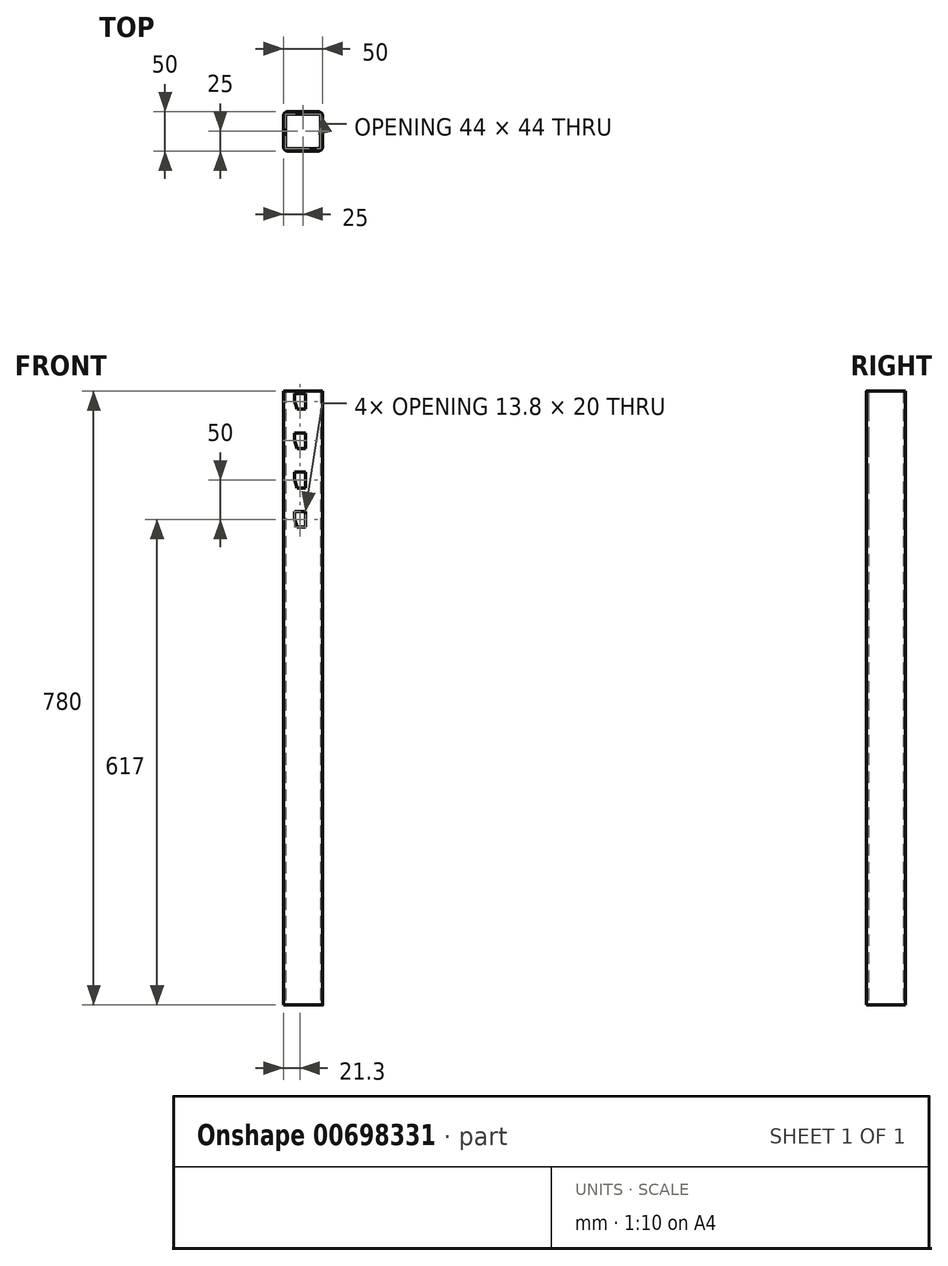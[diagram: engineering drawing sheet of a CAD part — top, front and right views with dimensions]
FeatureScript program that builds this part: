
annotation { "Feature Type Name" : "Feature", "Feature Type Description" : "" }
export const myFeature = defineFeature(function(context is Context, id is Id, definition is map)
    precondition{}
    {
        {
            var Q0;
            Q0=qCreatedBy(makeId("Top.planeOp"),FACE);
            var sketch = newSketch(context, id + "F0", { "sketchPlane" : qUnion([Q0])});
            skLineSegment(sketch, "E0.bottom", {"start": v(19, -25) * mm, "end": v(-19, -25) * mm});
            skLineSegment(sketch, "E0.top", {"start": v(19, 25) * mm, "end": v(-19, 25) * mm});
            skLineSegment(sketch, "E0.left", {"start": v(25, -19) * mm, "end": v(25, 19) * mm});
            skLineSegment(sketch, "E0.right", {"start": v(-25, -19) * mm, "end": v(-25, 19) * mm});
            skPoint(sketch, "E0.middle", {"position": v(0, 0) * mm});
            skLineSegment(sketch, "E1.bottom", {"start": v(19, 22) * mm, "end": v(-19, 22) * mm});
            skLineSegment(sketch, "E1.top", {"start": v(19, -22) * mm, "end": v(-19, -22) * mm});
            skLineSegment(sketch, "E1.left", {"start": v(22, 19) * mm, "end": v(22, -19) * mm});
            skLineSegment(sketch, "E1.right", {"start": v(-22, 19) * mm, "end": v(-22, -19) * mm});
            skPoint(sketch, "E2.visualSharp", {"position": v(-25, -25) * mm});
            skArc(sketch, "E2.filletArc", {"start": v(-25, -19) * mm, "mid": v(-23.24, -23.24) * mm, "end": v(-19, -25) * mm});
            skPoint(sketch, "E3.visualSharp", {"position": v(25, -25) * mm});
            skArc(sketch, "E3.filletArc", {"start": v(19, -25) * mm, "mid": v(23.24, -23.24) * mm, "end": v(25, -19) * mm});
            skPoint(sketch, "E4.visualSharp", {"position": v(25, 25) * mm});
            skArc(sketch, "E4.filletArc", {"start": v(25, 19) * mm, "mid": v(23.24, 23.24) * mm, "end": v(19, 25) * mm});
            skPoint(sketch, "E5.visualSharp", {"position": v(-25, 25) * mm});
            skArc(sketch, "E5.filletArc", {"start": v(-19, 25) * mm, "mid": v(-23.24, 23.24) * mm, "end": v(-25, 19) * mm});
            skPoint(sketch, "E6.visualSharp", {"position": v(-22, 22) * mm});
            skArc(sketch, "E6.filletArc", {"start": v(-19, 22) * mm, "mid": v(-21.12, 21.12) * mm, "end": v(-22, 19) * mm});
            skPoint(sketch, "E7.visualSharp", {"position": v(22, 22) * mm});
            skArc(sketch, "E7.filletArc", {"start": v(22, 19) * mm, "mid": v(21.12, 21.12) * mm, "end": v(19, 22) * mm});
            skPoint(sketch, "E8.visualSharp", {"position": v(22, -22) * mm});
            skArc(sketch, "E8.filletArc", {"start": v(19, -22) * mm, "mid": v(21.12, -21.12) * mm, "end": v(22, -19) * mm});
            skPoint(sketch, "E9.visualSharp", {"position": v(-22, -22) * mm});
            skArc(sketch, "E9.filletArc", {"start": v(-22, -19) * mm, "mid": v(-21.12, -21.12) * mm, "end": v(-19, -22) * mm});
            skSolve(sketch);
        }
        {
            var Q0;
            Q0=makeQuery(id+"F0.imprint","IMPRINT",FACE,{"disambiguationData":[TD([[makeQuery(id+"F0.imprint","IMPRINT",EDGE,{"derivedFrom":sQuery(id+"F0.wireOp",EDGE,"E0.bottom")}),-1.0]])]});
            extrude(context, id + "F1", {"entities" : qUnion([Q0]), "depth" : 780 * mm, "offsetDistance" : 25 * mm});
        }
        {
            var Q0;
            Q0=makeQuery(id+"F1.opExtrude","SWEPT_FACE",FACE,{"disambiguationData":[OSD([sQuery(id+"F0.wireOp",EDGE,"E0.bottom")])]});
            var sketch = newSketch(context, id + "F2", { "sketchPlane" : qUnion([Q0])});
            skLineSegment(sketch, "E10", {"start": v(-10.6, 777) * mm, "end": v(3.2, 777) * mm});
            skLineSegment(sketch, "E11", {"start": v(3.2, 757) * mm, "end": v(3.2, 777) * mm});
            skPoint(sketch, "E12.orphan", {"position": v(-10.6, 756.54) * mm});
            skLineSegment(sketch, "E13", {"start": v(-10.6, 777) * mm, "end": v(-10.6, 768) * mm});
            skLineSegment(sketch, "E14", {"start": v(-10.6, 768) * mm, "end": v(-7.6, 757) * mm});
            skLineSegment(sketch, "E15", {"start": v(-7.6, 757) * mm, "end": v(3.2, 757) * mm});
            skLineSegment(sketch, "E16.0.1.0", {"start": v(-10.6, 718) * mm, "end": v(-7.6, 707) * mm});
            skLineSegment(sketch, "E16.0.1.1", {"start": v(-10.6, 727) * mm, "end": v(-10.6, 718) * mm});
            skLineSegment(sketch, "E16.0.1.2", {"start": v(-10.6, 727) * mm, "end": v(3.2, 727) * mm});
            skLineSegment(sketch, "E16.0.1.3", {"start": v(3.2, 707) * mm, "end": v(3.2, 727) * mm});
            skLineSegment(sketch, "E16.0.1.4", {"start": v(-7.6, 707) * mm, "end": v(3.2, 707) * mm});
            skLineSegment(sketch, "E16.0.2.0", {"start": v(-10.6, 668) * mm, "end": v(-7.6, 657) * mm});
            skLineSegment(sketch, "E16.0.2.1", {"start": v(-10.6, 677) * mm, "end": v(-10.6, 668) * mm});
            skLineSegment(sketch, "E16.0.2.2", {"start": v(-10.6, 677) * mm, "end": v(3.2, 677) * mm});
            skLineSegment(sketch, "E16.0.2.3", {"start": v(3.2, 657) * mm, "end": v(3.2, 677) * mm});
            skLineSegment(sketch, "E16.0.2.4", {"start": v(-7.6, 657) * mm, "end": v(3.2, 657) * mm});
            skLineSegment(sketch, "E16.0.3.0", {"start": v(-10.6, 618) * mm, "end": v(-7.6, 607) * mm});
            skLineSegment(sketch, "E16.0.3.1", {"start": v(-10.6, 627) * mm, "end": v(-10.6, 618) * mm});
            skLineSegment(sketch, "E16.0.3.2", {"start": v(-10.6, 627) * mm, "end": v(3.2, 627) * mm});
            skLineSegment(sketch, "E16.0.3.3", {"start": v(3.2, 607) * mm, "end": v(3.2, 627) * mm});
            skLineSegment(sketch, "E16.0.3.4", {"start": v(-7.6, 607) * mm, "end": v(3.2, 607) * mm});
            skLineSegment(sketch, "E16.direction1", {"start": v(-7.6, 757) * mm, "end": v(17.4, 757) * mm, "construction": true});
            skLineSegment(sketch, "E16.direction2", {"start": v(-7.6, 757) * mm, "end": v(-7.6, 707) * mm, "construction": true});
            skSolve(sketch);
        }
        {
            var Q0;
            Q0=makeQuery(id+"F2.imprint","IMPRINT",FACE,{"disambiguationData":[TD([[makeQuery(id+"F2.imprint","IMPRINT",EDGE,{"derivedFrom":sQuery(id+"F2.wireOp",EDGE,"E10")}),-1.0]])]});
            var Q1;
            Q1=makeQuery(id+"F2.imprint","IMPRINT",FACE,{"disambiguationData":[TD([[makeQuery(id+"F2.imprint","IMPRINT",EDGE,{"derivedFrom":sQuery(id+"F2.wireOp",EDGE,"E16.0.1.0")}),1.0]])]});
            var Q2;
            Q2=makeQuery(id+"F2.imprint","IMPRINT",FACE,{"disambiguationData":[TD([[makeQuery(id+"F2.imprint","IMPRINT",EDGE,{"derivedFrom":sQuery(id+"F2.wireOp",EDGE,"E16.0.2.0")}),1.0]])]});
            var Q3;
            Q3=makeQuery(id+"F2.imprint","IMPRINT",FACE,{"disambiguationData":[TD([[makeQuery(id+"F2.imprint","IMPRINT",EDGE,{"derivedFrom":sQuery(id+"F2.wireOp",EDGE,"E16.0.3.0")}),1.0]])]});
            extrude(context, id + "F3", {"entities" : qUnion([Q0, Q1, Q2, Q3]), "operationType" : NewBodyOperationType.REMOVE, "oppositeDirection" : true, "depth" : 3 * mm, "offsetDistance" : 25 * mm});
        }
    });
